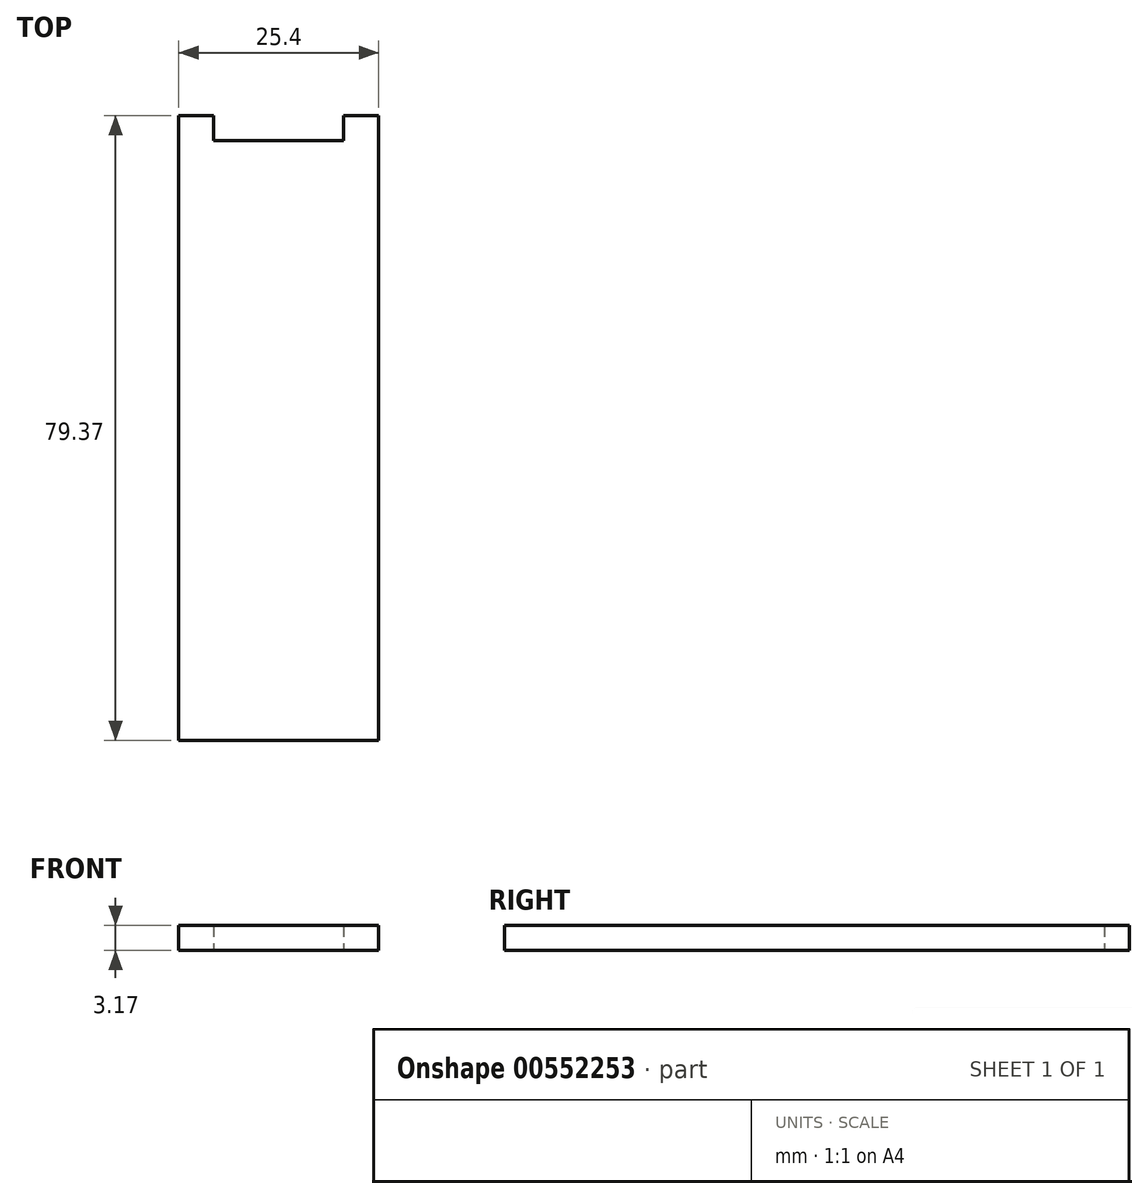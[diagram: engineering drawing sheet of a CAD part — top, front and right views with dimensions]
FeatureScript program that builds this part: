
annotation { "Feature Type Name" : "Feature", "Feature Type Description" : "" }
export const myFeature = defineFeature(function(context is Context, id is Id, definition is map)
    precondition{}
    {
        {
            var Q0;
            Q0=qCreatedBy(makeId("Top.planeOp"),FACE);
            var sketch = newSketch(context, id + "F0", { "sketchPlane" : qUnion([Q0])});
            skLineSegment(sketch, "E0.top", {"start": v(12.7, -38.1) * mm, "end": v(-12.7, -38.1) * mm});
            skLineSegment(sketch, "E0.left", {"start": v(12.7, 38.1) * mm, "end": v(12.7, -38.1) * mm});
            skLineSegment(sketch, "E0.right", {"start": v(-12.7, 38.1) * mm, "end": v(-12.7, -38.1) * mm});
            skPoint(sketch, "E0.middle", {"position": v(0, 0) * mm});
            skLineSegment(sketch, "E1", {"start": v(12.7, 38.1) * mm, "end": v(12.7, 41.27) * mm});
            skLineSegment(sketch, "E2.left", {"start": v(-12.7, 38.1) * mm, "end": v(-12.7, 41.27) * mm});
            skLineSegment(sketch, "E3.left", {"start": v(8.26, 38.1) * mm, "end": v(8.26, 41.27) * mm});
            skLineSegment(sketch, "E4", {"start": v(-8.26, 41.27) * mm, "end": v(-8.26, 38.1) * mm});
            skLineSegment(sketch, "E5", {"start": v(-8.26, 38.1) * mm, "end": v(8.26, 38.1) * mm});
            skLineSegment(sketch, "E6", {"start": v(8.26, 41.27) * mm, "end": v(12.7, 41.27) * mm});
            skLineSegment(sketch, "E7", {"start": v(-8.26, 41.27) * mm, "end": v(-12.7, 41.27) * mm});
            skSolve(sketch);
        }
        {
            var Q0;
            Q0=makeQuery(id+"F0.imprint","IMPRINT",FACE,{"disambiguationData":[TD([[makeQuery(id+"F0.imprint","IMPRINT",EDGE,{"derivedFrom":sQuery(id+"F0.wireOp",EDGE,"E0.top")}),-1.0]])]});
            extrude(context, id + "F1", {"entities" : qUnion([Q0]), "depth" : 3.17 * mm, "offsetDistance" : 25.4 * mm});
        }
    });
